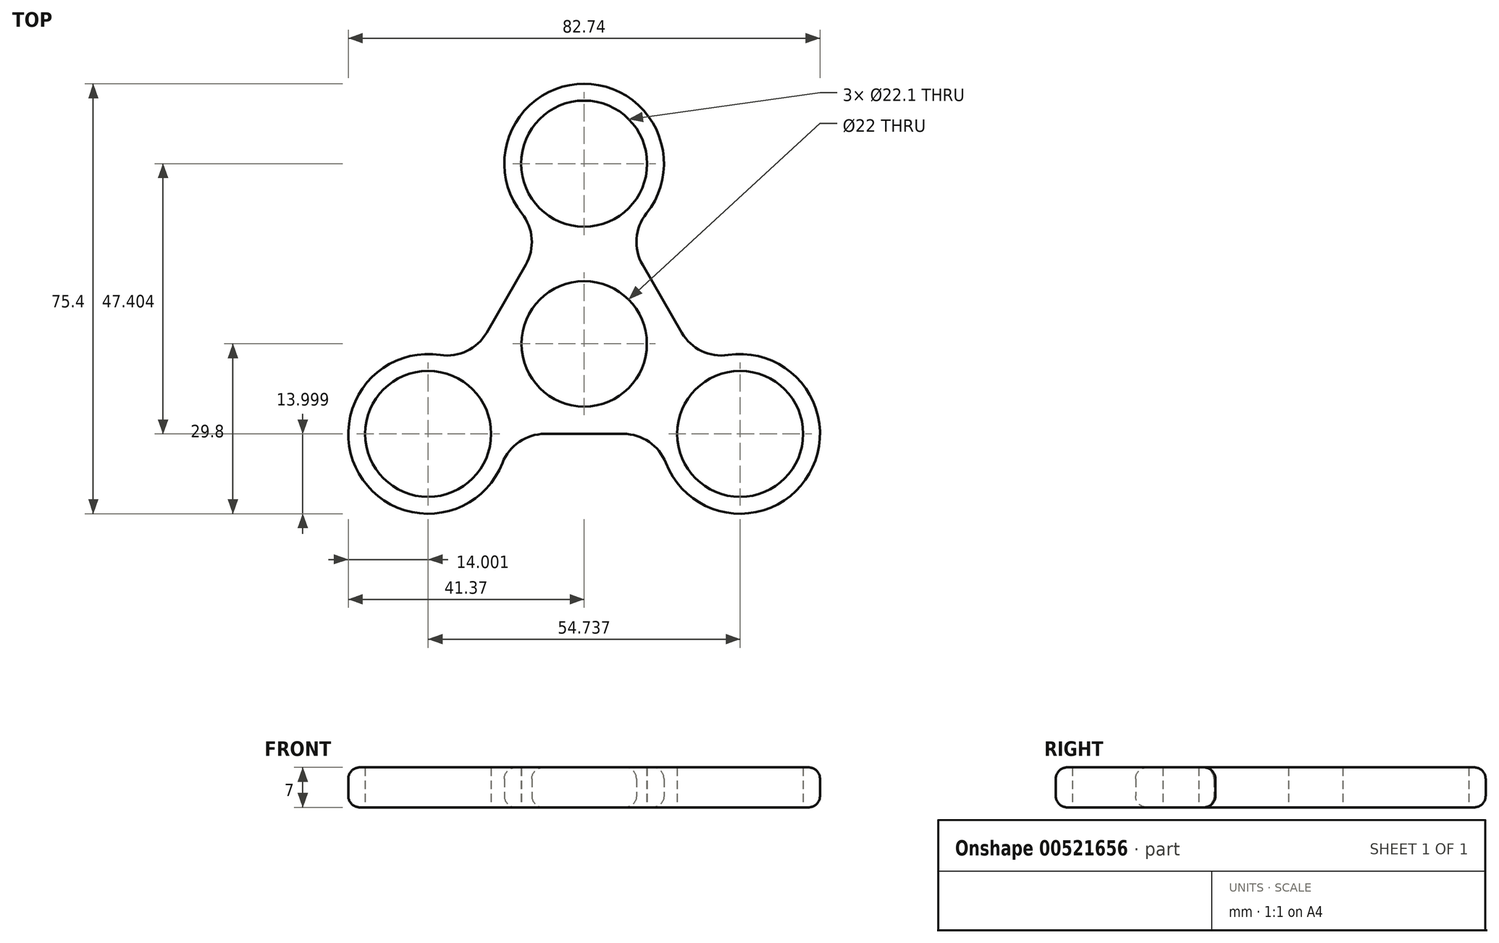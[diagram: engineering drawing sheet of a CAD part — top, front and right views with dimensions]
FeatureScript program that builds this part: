
annotation { "Feature Type Name" : "Feature", "Feature Type Description" : "" }
export const myFeature = defineFeature(function(context is Context, id is Id, definition is map)
    precondition{}
    {
        {
            var Q0;
            Q0=qCreatedBy(makeId("Top.planeOp"),FACE);
            var sketch = newSketch(context, id + "F0", { "sketchPlane" : qUnion([Q0])});
            skCircle(sketch, "E0", {"center": v(0, 31.6) * mm, "radius": 11.05 * mm});
            skCircle(sketch, "E1.1.0", {"center": v(-27.37, -15.8) * mm, "radius": 11.05 * mm});
            skCircle(sketch, "E1.2.0", {"center": v(27.37, -15.8) * mm, "radius": 11.05 * mm});
            skPoint(sketch, "E1.center", {"position": v(0, 0) * mm});
            skCircle(sketch, "E2", {"center": v(0, 31.6) * mm, "radius": 14 * mm});
            skCircle(sketch, "E3.1.0", {"center": v(-27.37, -15.8) * mm, "radius": 14 * mm});
            skCircle(sketch, "E3.2.0", {"center": v(27.37, -15.8) * mm, "radius": 14 * mm});
            skCircle(sketch, "E4", {"center": v(0, 0) * mm, "radius": 11 * mm});
            skCircle(sketch, "E5", {"center": v(0, 0) * mm, "radius": 14 * mm, "construction": true});
            skLineSegment(sketch, "E6", {"start": v(-27.37, -15.8) * mm, "end": v(0, 31.6) * mm});
            skLineSegment(sketch, "E7", {"start": v(0, 31.6) * mm, "end": v(27.37, -15.8) * mm});
            skLineSegment(sketch, "E8", {"start": v(27.37, -15.8) * mm, "end": v(-27.37, -15.8) * mm});
            skPoint(sketch, "E9", {"position": v(0, 45.6) * mm});
            skSolve(sketch);
        }
        {
            var Q0;
            Q0 = qSketchRegion(id + "F0", true);
            extrude(context, id + "F1", {"entities" : qUnion([Q0]), "endBound" : BoundingType.SYMMETRIC, "depth" : 7 * mm, "offsetDistance" : 25 * mm});
        }
        {
            var Q0;
            Q0=makeQuery(id+"F1.opExtrude","SWEPT_EDGE",EDGE,{"disambiguationData":[OSD([sQuery(id+"F0.wireOp",EDGE,"E3.2.0"),sQuery(id+"F0.wireOp",EDGE,"zSg69FSz-ja27-GQGE-MR0P-PLYQZ15IPlXa")])]});
            var Q1;
            Q1=makeQuery(id+"F1.opExtrude","SWEPT_EDGE",EDGE,{"disambiguationData":[OSD([sQuery(id+"F0.wireOp",EDGE,"E2"),sQuery(id+"F0.wireOp",EDGE,"zSg69FSz-ja27-GQGE-MR0P-PLYQZ15IPlXa")])]});
            var Q2;
            Q2=makeQuery(id+"F1.opExtrude","SWEPT_EDGE",EDGE,{"disambiguationData":[OSD([sQuery(id+"F0.wireOp",EDGE,"E2"),sQuery(id+"F0.wireOp",EDGE,"oBNQ3VcD-oVfM-tYSh-CwtA-rd2oLKiVvI6k")])]});
            var Q3;
            Q3=makeQuery(id+"F1.opExtrude","SWEPT_EDGE",EDGE,{"disambiguationData":[OSD([sQuery(id+"F0.wireOp",EDGE,"E3.2.0"),sQuery(id+"F0.wireOp",EDGE,"oS4GqZWx-UiGZ-MHNm-b1dr-cg6UlFnWGaa9")])]});
            var Q4;
            Q4=makeQuery(id+"F1.opExtrude","SWEPT_EDGE",EDGE,{"disambiguationData":[OSD([sQuery(id+"F0.wireOp",EDGE,"E3.1.0"),sQuery(id+"F0.wireOp",EDGE,"oBNQ3VcD-oVfM-tYSh-CwtA-rd2oLKiVvI6k")])]});
            var Q5;
            Q5=makeQuery(id+"F1.opExtrude","SWEPT_EDGE",EDGE,{"disambiguationData":[OSD([sQuery(id+"F0.wireOp",EDGE,"E3.1.0"),sQuery(id+"F0.wireOp",EDGE,"oS4GqZWx-UiGZ-MHNm-b1dr-cg6UlFnWGaa9")])]});
            fillet(context, id + "F2", {"entities" : qUnion([Q0, Q1, Q2, Q3, Q4, Q5]), "radius" : 8 * mm, "tangentPropagation" : true, "allowEdgeOverflow" : false});
        }
        {
            var Q0;
            Q0=makeQuery(id+"F1.opExtrude","CAP_EDGE",EDGE,{"disambiguationData":[OSD([sQuery(id+"F0.wireOp",EDGE,"E3.1.0")])],"isStart":false});
            var Q1;
            Q1=makeQuery(id+"F1.opExtrude","CAP_EDGE",EDGE,{"disambiguationData":[OSD([sQuery(id+"F0.wireOp",EDGE,"E3.1.0")])],"isStart":true});
            fillet(context, id + "F3", {"entities" : qUnion([Q0, Q1]), "radius" : 2 * mm, "tangentPropagation" : true, "allowEdgeOverflow" : false});
        }
    });
